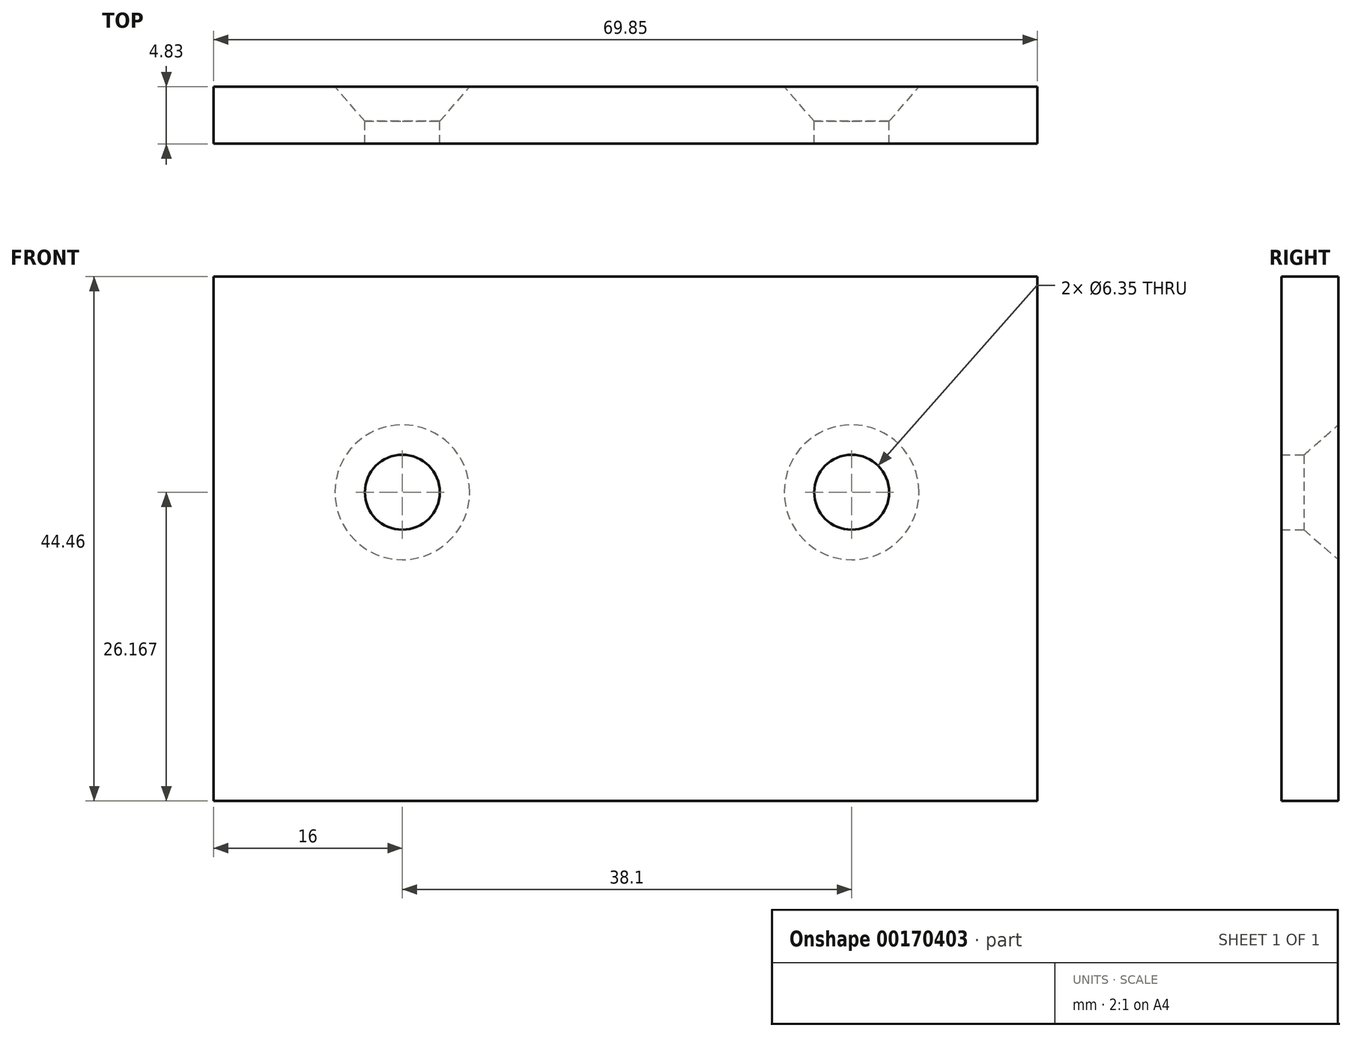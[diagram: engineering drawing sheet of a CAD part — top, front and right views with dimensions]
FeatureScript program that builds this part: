
annotation { "Feature Type Name" : "Feature", "Feature Type Description" : "" }
export const myFeature = defineFeature(function(context is Context, id is Id, definition is map)
    precondition{}
    {
        {
            var Q0;
            Q0=qCreatedBy(makeId("Front.planeOp"),FACE);
            var sketch = newSketch(context, id + "F0", { "sketchPlane" : qUnion([Q0])});
            skLineSegment(sketch, "E0.bottom", {"start": v(-35.05, 22.23) * mm, "end": v(34.8, 22.23) * mm});
            skLineSegment(sketch, "E0.top", {"start": v(-35.05, -22.23) * mm, "end": v(34.8, -22.23) * mm});
            skLineSegment(sketch, "E0.left", {"start": v(-35.05, 22.22) * mm, "end": v(-35.05, -22.23) * mm});
            skLineSegment(sketch, "E0.right", {"start": v(34.8, 22.23) * mm, "end": v(34.8, -22.23) * mm});
            skPoint(sketch, "E1", {"position": v(-19.05, 3.94) * mm});
            skPoint(sketch, "E2", {"position": v(19.05, 3.94) * mm});
            skSolve(sketch);
        }
        {
            var Q0;
            Q0 = qSketchRegion(id + "F0", true);
            extrude(context, id + "F1", {"entities" : qUnion([Q0]), "depth" : 4.83 * mm});
        }
        {
            var Q0;
            Q0=sQuery(id+"F0.wireOp",VERTEX,"E1");
            var Q1;
            Q1=sQuery(id+"F0.wireOp",VERTEX,"E2");
            var Q2;
            Q2=makeQuery(id+"F1.opExtrude","SWEPT_BODY",BODY,{"disambiguationData":[OSD([sQuery(id+"F0.wireOp",EDGE,"E0.bottom"),sQuery(id+"F0.wireOp",EDGE,"E0.top"),sQuery(id+"F0.wireOp",EDGE,"E0.left"),sQuery(id+"F0.wireOp",EDGE,"E0.right")])]});
            hole(context, id + "F2", {"style" : HoleStyle.C_SINK, "endStyle" : HoleEndStyle.THROUGH, "oppositeDirection" : true, "holeDiameter" : 6.35 * mm, "cSinkDiameter" : 11.43 * mm, "cSinkAngle" : 82 * degree, "locations" : qUnion([Q0, Q1]), "scope" : qUnion([Q2]), "isTappedThrough" : true});
        }
    });
